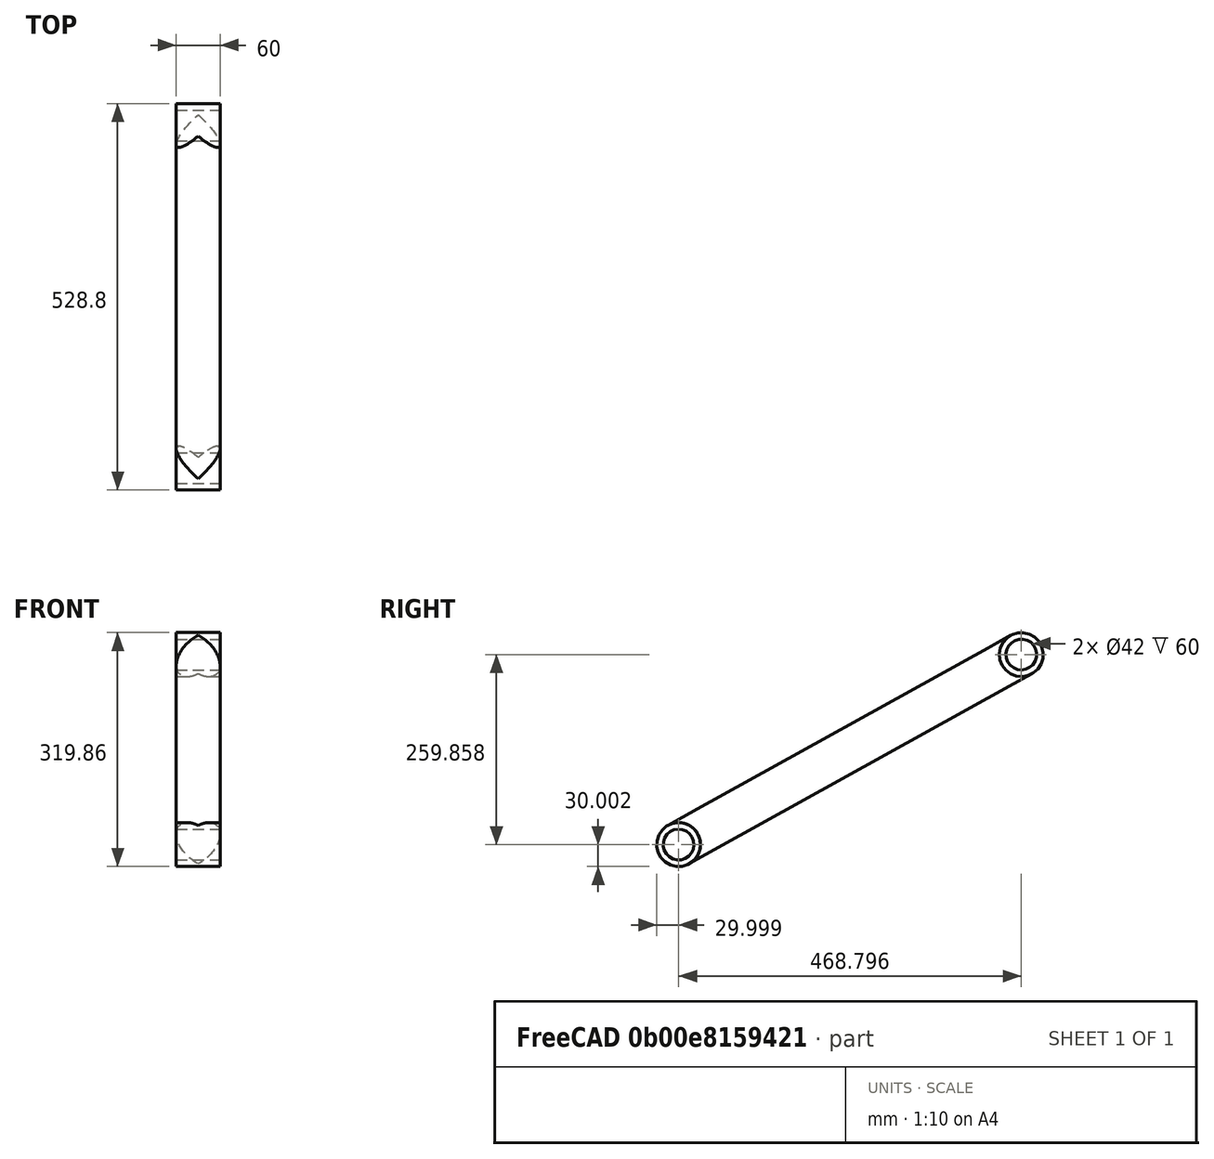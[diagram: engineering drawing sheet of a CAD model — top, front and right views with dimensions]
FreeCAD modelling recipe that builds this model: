
FCSTD DOCUMENT  (FreeCAD 0.16R6704 (Git))
Label: Tiejra
License: All rights reserved
LicenseURL: http://en.wikipedia.org/wiki/All_rights_reserved
objects: Part::Cylinder×6, Part::MultiFuse×3, Part::Cut×2
note: 11 computed .brp shape members not serialized (recipe doc carries the construction recipe); baked Part::Feature solids carry a one-line shape summary decoded from their .brp

FEATURE [Part::Cylinder] Cylinder054  label="Cilindro040"
  Angle = 360
  Height = 60
  Placement = pos=(0,30,0) rot=(1,0,0;1.5708rad)
  Radius = 30
FEATURE [Part::Cylinder] Cylinder055  label="Cilindro041"
  Angle = 360
  Height = 490
  Placement = pos=(0,0,0) rot=(0,1,0;1.5708rad)
  Radius = 30
FEATURE [Part::Cylinder] Cylinder056  label="Cilindro042"
  Angle = 360
  Height = 60
  Placement = pos=(0,30,0) rot=(1,0,0;1.5708rad)
  Radius = 21
FEATURE [Part::MultiFuse] Fusion024
  Shapes = -> [Cylinder055,Cylinder054]
FEATURE [Part::Cut] Cut057
  Base = -> Fusion024
  Placement = pos=(551,0,0) rot=(0,1,0;3.14159rad)
  Tool = -> Cylinder056
FEATURE [Part::Cylinder] Cylinder057  label="Cilindro043"
  Angle = 360
  Height = 60
  Placement = pos=(0,30,0) rot=(1,0,0;1.5708rad)
  Radius = 30
FEATURE [Part::Cylinder] Cylinder058  label="Cilindro044"
  Angle = 360
  Height = 500
  Placement = pos=(0,0,0) rot=(0,1,0;1.5708rad)
  Radius = 30
FEATURE [Part::Cylinder] Cylinder059  label="Cilindro045"
  Angle = 360
  Height = 60
  Placement = pos=(0,30,0) rot=(1,0,0;1.5708rad)
  Radius = 21
FEATURE [Part::MultiFuse] Fusion025
  Shapes = -> [Cylinder058,Cylinder057]
FEATURE [Part::Cut] Cut058
  Base = -> Fusion025
  Placement = pos=(15,0,0) rot=(0,0,1;0rad)
  Tool = -> Cylinder059
FEATURE [Part::MultiFuse] Fusion026
  Placement = pos=(-191,-17,-5) rot=(0.242883,-0.242883,0.939157;1.63353rad)
  Shapes = -> [Cut058,Cut057]
